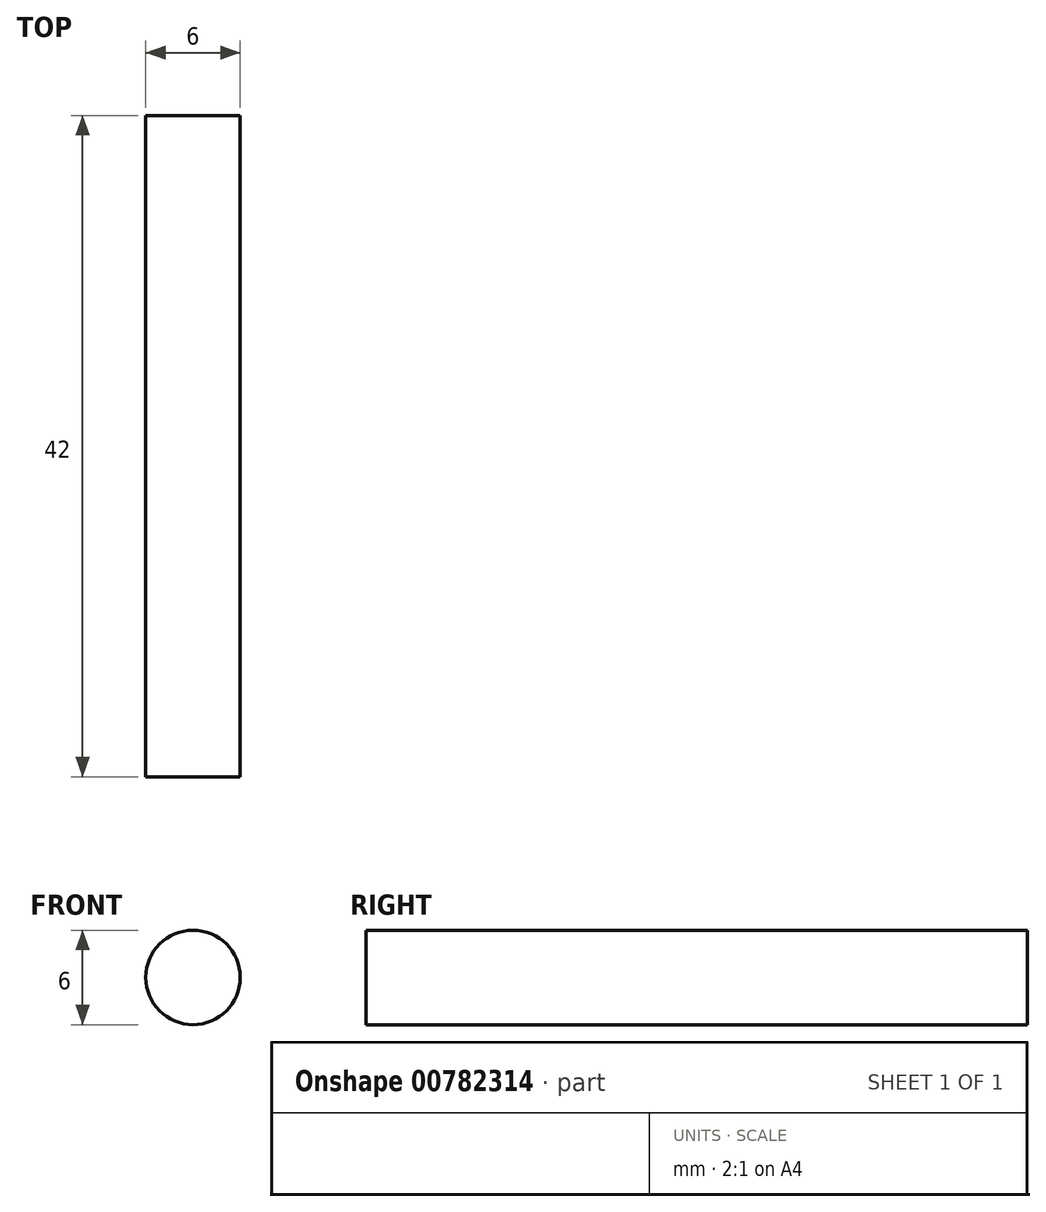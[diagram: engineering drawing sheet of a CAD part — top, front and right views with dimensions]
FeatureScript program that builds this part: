
annotation { "Feature Type Name" : "Feature", "Feature Type Description" : "" }
export const myFeature = defineFeature(function(context is Context, id is Id, definition is map)
    precondition{}
    {
        {
            var Q0;
            Q0=qCreatedBy(makeId("Front.planeOp"),FACE);
            var sketch = newSketch(context, id + "F0", { "sketchPlane" : qUnion([Q0])});
            skCircle(sketch, "E0", {"center": v(0, 0) * mm, "radius": 3 * mm});
            skSolve(sketch);
        }
        {
            var Q0;
            Q0 = qSketchRegion(id + "F0", true);
            extrude(context, id + "F1", {"entities" : qUnion([Q0]), "depth" : 42 * mm, "offsetDistance" : 25 * mm});
        }
    });
